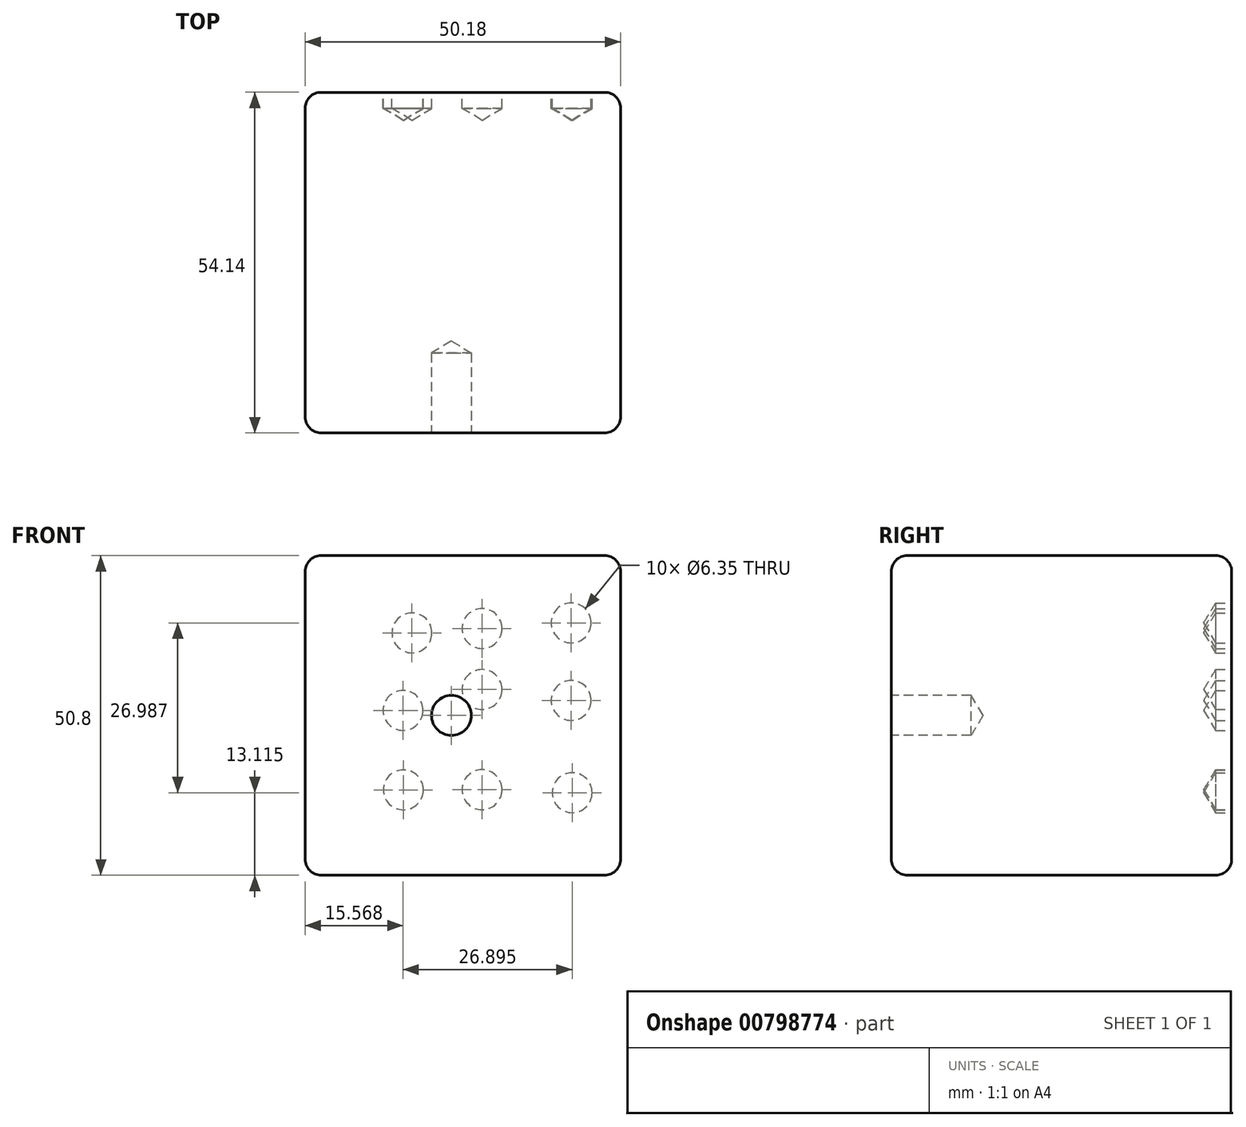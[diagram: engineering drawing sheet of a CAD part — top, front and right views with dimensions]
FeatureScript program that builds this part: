
annotation { "Feature Type Name" : "Feature", "Feature Type Description" : "" }
export const myFeature = defineFeature(function(context is Context, id is Id, definition is map)
    precondition{}
    {
        {
            var Q0;
            Q0=qCreatedBy(makeId("Top.planeOp"),FACE);
            var sketch = newSketch(context, id + "F0", { "sketchPlane" : qUnion([Q0])});
            skLineSegment(sketch, "E0.bottom", {"start": v(-28.13, 11.7) * mm, "end": v(22.05, 11.7) * mm});
            skLineSegment(sketch, "E0.top", {"start": v(-28.13, -42.44) * mm, "end": v(22.05, -42.44) * mm});
            skLineSegment(sketch, "E0.left", {"start": v(-28.13, 11.7) * mm, "end": v(-28.13, -42.44) * mm});
            skLineSegment(sketch, "E0.right", {"start": v(22.05, 11.7) * mm, "end": v(22.05, -42.44) * mm});
            skSolve(sketch);
        }
        {
            var Q0;
            Q0 = qSketchRegion(id + "F0", true);
            extrude(context, id + "F1", {"entities" : qUnion([Q0]), "depth" : 50.8 * mm, "offsetDistance" : 25.4 * mm});
        }
        {
            var Q0;
            Q0=makeQuery(id+"F1.opExtrude","SWEPT_FACE",FACE,{"disambiguationData":[OSD([sQuery(id+"F0.wireOp",EDGE,"E0.top")])]});
            var sketch = newSketch(context, id + "F2", { "sketchPlane" : qUnion([Q0])});
            skPoint(sketch, "E1", {"position": v(-4.86, 25.4) * mm});
            skPoint(sketch, "E1.positionSnap0", {"position": v(22.05, 25.4) * mm});
            skSolve(sketch);
        }
        {
            var Q0;
            Q0=sQuery(id+"F2.wireOp",VERTEX,"E1");
            var Q1;
            Q1=makeQuery(id+"F1.opExtrude","SWEPT_BODY",BODY,{"disambiguationData":[OSD([sQuery(id+"F0.wireOp",EDGE,"E0.bottom"),sQuery(id+"F0.wireOp",EDGE,"E0.top"),sQuery(id+"F0.wireOp",EDGE,"E0.left"),sQuery(id+"F0.wireOp",EDGE,"E0.right")])]});
            hole(context, id + "F3", {"style" : HoleStyle.SIMPLE, "endStyle" : HoleEndStyle.BLIND, "holeDiameter" : 6.35 * mm, "majorDiameter" : 6.35 * mm, "holeDepth" : 12.7 * mm, "isTappedThrough" : true, "tappedDepth" : 12.7 * mm, "tapClearance" : 3, "startFromSketch" : true, "locations" : qUnion([Q0]), "scope" : qUnion([Q1])});
        }
        {
            var Q0;
            Q0=makeQuery(id+"F1.opExtrude","SWEPT_FACE",FACE,{"disambiguationData":[OSD([sQuery(id+"F0.wireOp",EDGE,"E0.bottom")])]});
            var sketch = newSketch(context, id + "F4", { "sketchPlane" : qUnion([Q0])});
            skPoint(sketch, "E2", {"position": v(12.52, 13.57) * mm});
            skPoint(sketch, "E3", {"position": v(0, 13.6) * mm});
            skPoint(sketch, "E4", {"position": v(-14.33, 13.12) * mm});
            skPoint(sketch, "E5", {"position": v(12.56, 26.19) * mm});
            skPoint(sketch, "E6", {"position": v(0, 29.5) * mm});
            skPoint(sketch, "E7", {"position": v(-14.18, 27.78) * mm});
            skPoint(sketch, "E8", {"position": v(11.14, 38.51) * mm});
            skPoint(sketch, "E9", {"position": v(0, 39.2) * mm});
            skPoint(sketch, "E10", {"position": v(-14.18, 40.1) * mm});
            skSolve(sketch);
        }
        {
            var Q0;
            Q0=sQuery(id+"F4.wireOp",VERTEX,"E2");
            var Q1;
            Q1=sQuery(id+"F4.wireOp",VERTEX,"E3");
            var Q2;
            Q2=sQuery(id+"F4.wireOp",VERTEX,"E4");
            var Q3;
            Q3=sQuery(id+"F4.wireOp",VERTEX,"E7");
            var Q4;
            Q4=sQuery(id+"F4.wireOp",VERTEX,"E6");
            var Q5;
            Q5=sQuery(id+"F4.wireOp",VERTEX,"E5");
            var Q6;
            Q6=sQuery(id+"F4.wireOp",VERTEX,"E8");
            var Q7;
            Q7=sQuery(id+"F4.wireOp",VERTEX,"E9");
            var Q8;
            Q8=sQuery(id+"F4.wireOp",VERTEX,"E10");
            var Q9;
            Q9=makeQuery(id+"F1.opExtrude","SWEPT_BODY",BODY,{"disambiguationData":[OSD([sQuery(id+"F0.wireOp",EDGE,"E0.bottom"),sQuery(id+"F0.wireOp",EDGE,"E0.top"),sQuery(id+"F0.wireOp",EDGE,"E0.left"),sQuery(id+"F0.wireOp",EDGE,"E0.right")])]});
            hole(context, id + "F5", {"style" : HoleStyle.SIMPLE, "endStyle" : HoleEndStyle.BLIND, "holeDiameter" : 6.35 * mm, "majorDiameter" : 6.35 * mm, "holeDepth" : 2.54 * mm, "isTappedThrough" : true, "tappedDepth" : 12.7 * mm, "tapClearance" : 3, "startFromSketch" : true, "locations" : qUnion([Q0, Q1, Q2, Q3, Q4, Q5, Q6, Q7, Q8]), "scope" : qUnion([Q9])});
        }
        {
            var Q0;
            Q0=makeQuery(id+"F1.opExtrude","CAP_EDGE",EDGE,{"disambiguationData":[OSD([sQuery(id+"F0.wireOp",EDGE,"E0.right")])],"isStart":false});
            var Q1;
            Q1=makeQuery(id+"F1.opExtrude","CAP_EDGE",EDGE,{"disambiguationData":[OSD([sQuery(id+"F0.wireOp",EDGE,"E0.bottom")])],"isStart":false});
            var Q2;
            Q2=makeQuery(id+"F1.opExtrude","CAP_EDGE",EDGE,{"disambiguationData":[OSD([sQuery(id+"F0.wireOp",EDGE,"E0.left")])],"isStart":false});
            var Q3;
            Q3=makeQuery(id+"F1.opExtrude","CAP_EDGE",EDGE,{"disambiguationData":[OSD([sQuery(id+"F0.wireOp",EDGE,"E0.top")])],"isStart":false});
            var Q4;
            Q4=makeQuery(id+"F1.opExtrude","SWEPT_EDGE",EDGE,{"disambiguationData":[OSD([sQuery(id+"F0.wireOp",EDGE,"E0.bottom"),sQuery(id+"F0.wireOp",EDGE,"E0.right")])]});
            var Q5;
            Q5=makeQuery(id+"F1.opExtrude","SWEPT_EDGE",EDGE,{"disambiguationData":[OSD([sQuery(id+"F0.wireOp",EDGE,"E0.top"),sQuery(id+"F0.wireOp",EDGE,"E0.right")])]});
            var Q6;
            Q6=makeQuery(id+"F1.opExtrude","CAP_EDGE",EDGE,{"disambiguationData":[OSD([sQuery(id+"F0.wireOp",EDGE,"E0.right")])],"isStart":true});
            var Q7;
            Q7=makeQuery(id+"F1.opExtrude","CAP_EDGE",EDGE,{"disambiguationData":[OSD([sQuery(id+"F0.wireOp",EDGE,"E0.top")])],"isStart":true});
            var Q8;
            Q8=makeQuery(id+"F1.opExtrude","CAP_EDGE",EDGE,{"disambiguationData":[OSD([sQuery(id+"F0.wireOp",EDGE,"E0.left")])],"isStart":true});
            var Q9;
            Q9=makeQuery(id+"F1.opExtrude","SWEPT_EDGE",EDGE,{"disambiguationData":[OSD([sQuery(id+"F0.wireOp",EDGE,"E0.bottom"),sQuery(id+"F0.wireOp",EDGE,"E0.left")])]});
            var Q10;
            Q10=makeQuery(id+"F1.opExtrude","CAP_EDGE",EDGE,{"disambiguationData":[OSD([sQuery(id+"F0.wireOp",EDGE,"E0.bottom")])],"isStart":true});
            var Q11;
            Q11=makeQuery(id+"F1.opExtrude","SWEPT_EDGE",EDGE,{"disambiguationData":[OSD([sQuery(id+"F0.wireOp",EDGE,"E0.top"),sQuery(id+"F0.wireOp",EDGE,"E0.left")])]});
            fillet(context, id + "F6", {"entities" : qUnion([Q0, Q1, Q2, Q3, Q4, Q5, Q6, Q7, Q8, Q9, Q10, Q11]), "radius" : 2.54 * mm, "tangentPropagation" : true, "allowEdgeOverflow" : false});
        }
    });
